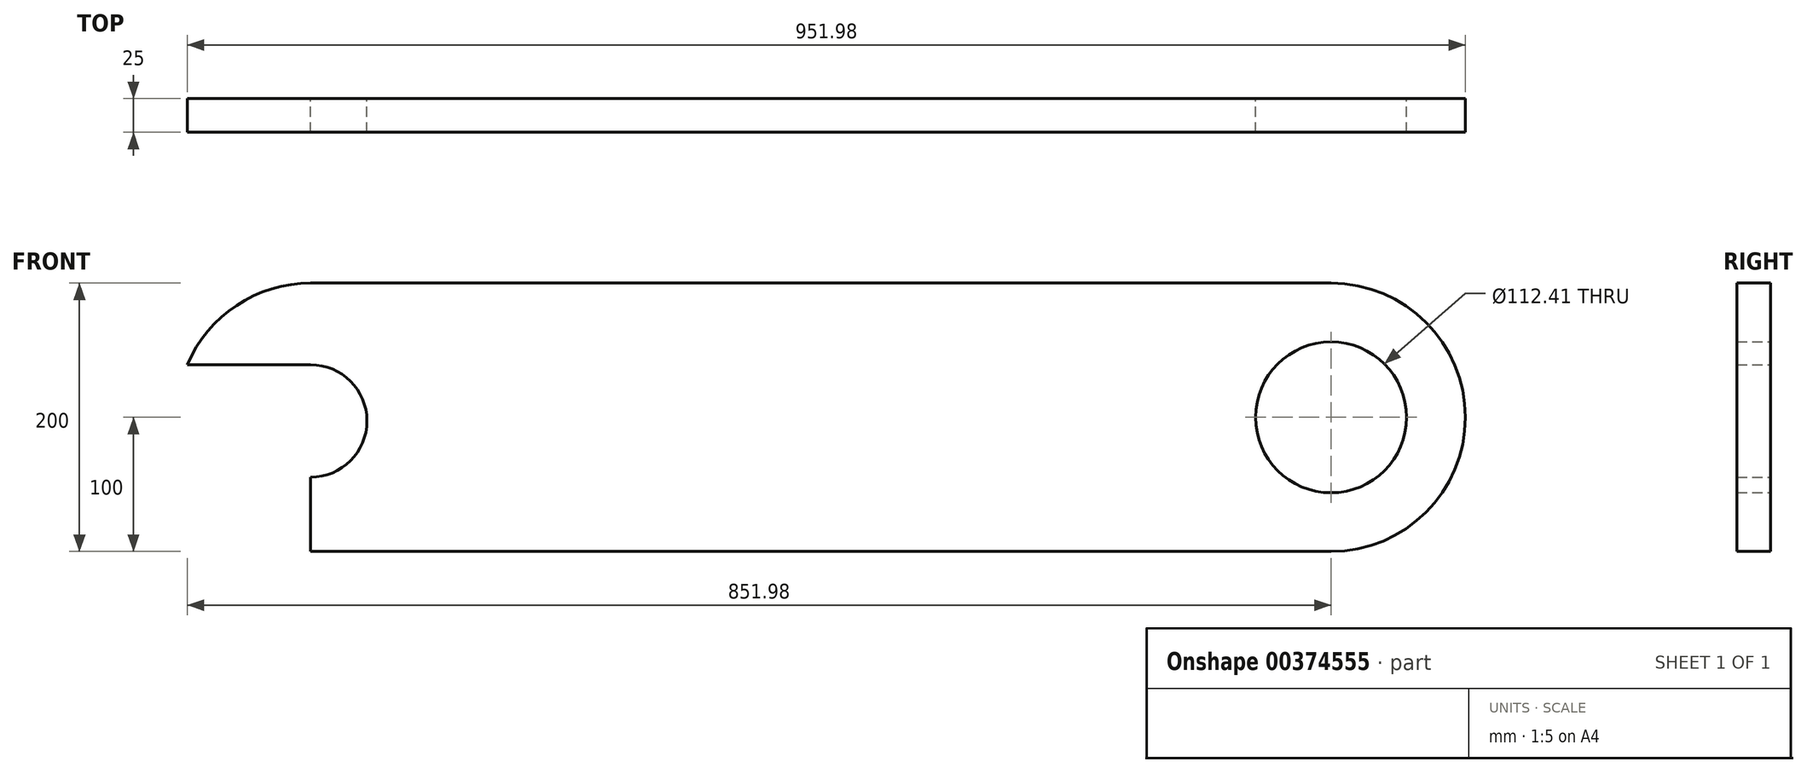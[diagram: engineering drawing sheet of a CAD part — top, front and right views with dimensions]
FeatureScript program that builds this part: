
annotation { "Feature Type Name" : "Feature", "Feature Type Description" : "" }
export const myFeature = defineFeature(function(context is Context, id is Id, definition is map)
    precondition{}
    {
        {
            var Q0;
            Q0=qCreatedBy(makeId("Front.planeOp"),FACE);
            var sketch = newSketch(context, id + "F0", { "sketchPlane" : qUnion([Q0])});
            skLineSegment(sketch, "E0.bottom", {"start": v(-190, 100) * mm, "end": v(190, 100) * mm});
            skLineSegment(sketch, "E0.top", {"start": v(-190, -100) * mm, "end": v(190, -100) * mm});
            skPoint(sketch, "E0.middle", {"position": v(0, 0) * mm});
            skArc(sketch, "E1", {"start": v(190, -100) * mm, "mid": v(290, 0) * mm, "end": v(190, 100) * mm});
            skLineSegment(sketch, "E2", {"start": v(-190, 100) * mm, "end": v(-570, 100) * mm});
            skLineSegment(sketch, "E3", {"start": v(-570, 100) * mm, "end": v(-570, 39.23) * mm});
            skLineSegment(sketch, "E4", {"start": v(-570, -100) * mm, "end": v(-190, -100) * mm});
            skArc(sketch, "E5", {"start": v(-570, 100) * mm, "mid": v(-625.12, 83.44) * mm, "end": v(-661.98, 39.23) * mm});
            skLineSegment(sketch, "E6", {"start": v(-661.98, 39.23) * mm, "end": v(-570, 39.23) * mm});
            skLineSegment(sketch, "E7", {"start": v(-570, 0) * mm, "end": v(-570, -2.7) * mm});
            skLineSegment(sketch, "E8", {"start": v(-570, -44.64) * mm, "end": v(-659.49, -44.64) * mm});
            skLineSegment(sketch, "E9", {"start": v(-659.49, -44.64) * mm, "end": v(-570, -44.64) * mm});
            skArc(sketch, "E10", {"start": v(-570, -44.64) * mm, "mid": v(-528.07, -2.7) * mm, "end": v(-570, 39.23) * mm});
            skArc(sketch, "E11.trimOffspring", {"start": v(-659.49, -44.64) * mm, "mid": v(-622.61, -85.04) * mm, "end": v(-570, -100) * mm});
            skLineSegment(sketch, "E12.trimOffspring", {"start": v(-570, -44.64) * mm, "end": v(-570, -100) * mm});
            skCircle(sketch, "E13", {"center": v(190, 0) * mm, "radius": 56.2 * mm});
            skSolve(sketch);
        }
        {
            var Q0;
            Q0=makeQuery(id+"F0.imprint","IMPRINT",FACE,{"disambiguationData":[TD([[makeQuery(id+"F0.imprint","IMPRINT",EDGE,{"derivedFrom":sQuery(id+"F0.wireOp",EDGE,"E0.bottom")}),-1.0]])]});
            var Q1;
            Q1=makeQuery(id+"F0.imprint","IMPRINT",FACE,{"disambiguationData":[TD([[makeQuery(id+"F0.imprint","IMPRINT",EDGE,{"derivedFrom":sQuery(id+"F0.wireOp",EDGE,"E3")}),-1.0]])]});
            var Q2;
            Q2=makeQuery(id+"F0.imprint","IMPRINT",FACE,{"disambiguationData":[TD([[makeQuery(id+"F0.imprint","IMPRINT",EDGE,{"derivedFrom":sQuery(id+"F0.wireOp",EDGE,"E9")}),-1.0]])]});
            extrude(context, id + "F1", {"entities" : qUnion([Q0, Q1, Q2]), "depth" : 25 * mm});
        }
    });
